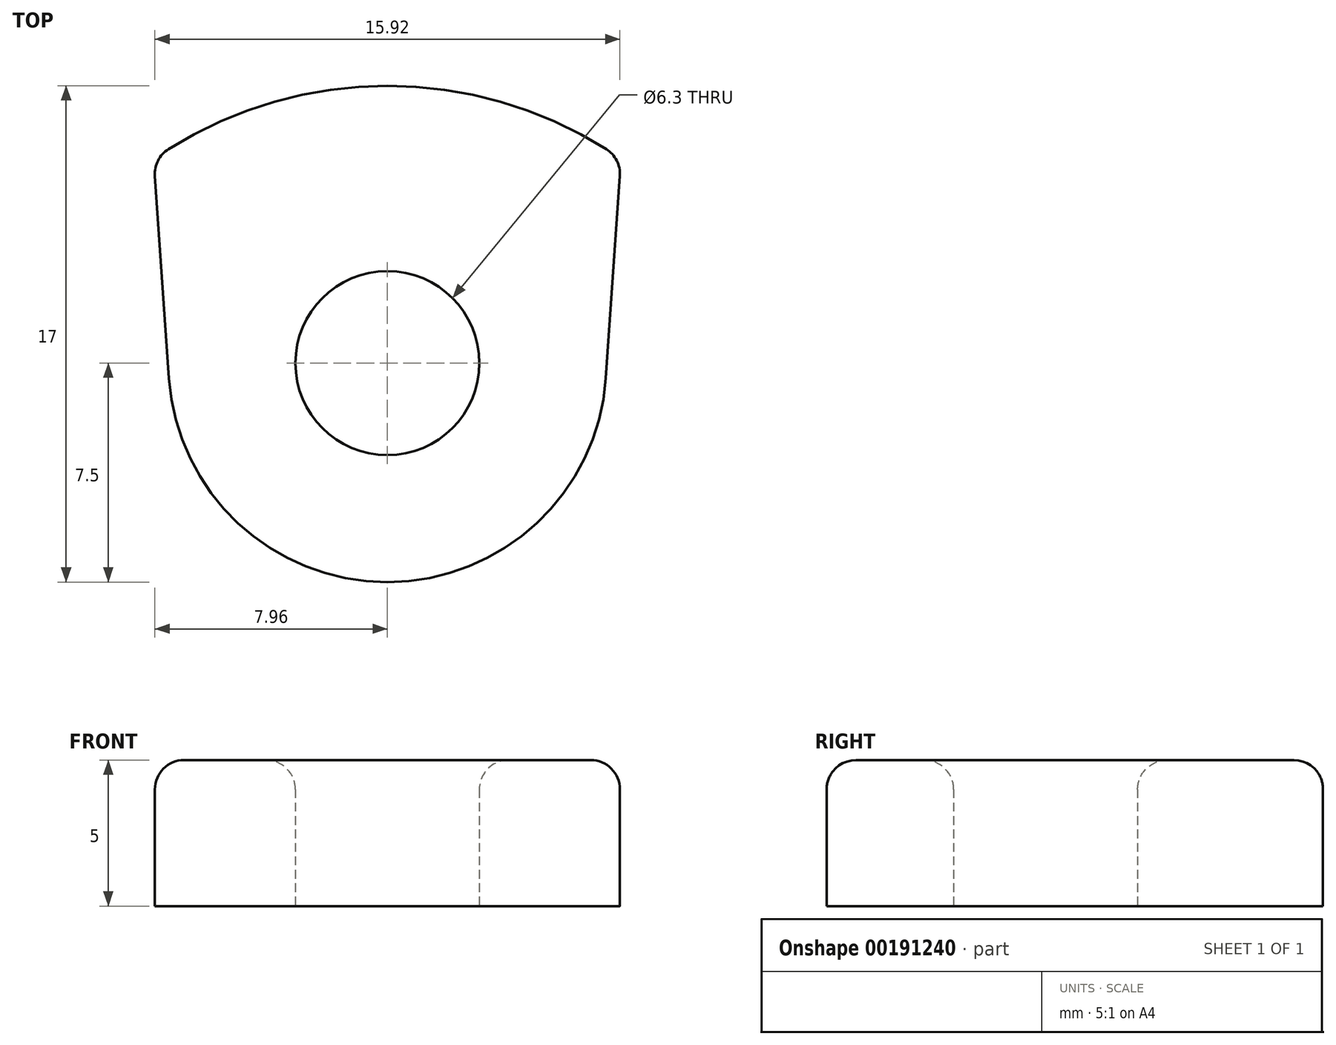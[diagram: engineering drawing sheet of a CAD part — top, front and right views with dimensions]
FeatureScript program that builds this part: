
annotation { "Feature Type Name" : "Feature", "Feature Type Description" : "" }
export const myFeature = defineFeature(function(context is Context, id is Id, definition is map)
    precondition{}
    {
        {
            var Q0;
            Q0=qCreatedBy(makeId("Top.planeOp"),FACE);
            var sketch = newSketch(context, id + "F0", { "sketchPlane" : qUnion([Q0])});
            skCircle(sketch, "E0", {"center": v(0, 0) * mm, "radius": 3.15 * mm});
            skArc(sketch, "E1", {"start": v(-7.48, -0.52) * mm, "mid": v(0, -7.5) * mm, "end": v(7.48, -0.52) * mm});
            skLineSegment(sketch, "E2", {"start": v(-8, 7) * mm, "end": v(0, 7) * mm, "construction": true});
            skLineSegment(sketch, "E3", {"start": v(-8, 7) * mm, "end": v(-7.48, -0.52) * mm});
            skLineSegment(sketch, "E4.MirrorCS", {"start": v(8, 7) * mm, "end": v(0, 7) * mm, "construction": true});
            skLineSegment(sketch, "E5.MirrorCS", {"start": v(8, 7) * mm, "end": v(7.48, -0.52) * mm});
            skLineSegment(sketch, "E6", {"start": v(0, 7) * mm, "end": v(0, 9.5) * mm, "construction": true});
            skArc(sketch, "E7", {"start": v(8, 7) * mm, "mid": v(0, 9.5) * mm, "end": v(-8, 7) * mm});
            skSolve(sketch);
        }
        {
            var Q0;
            Q0 = qSketchRegion(id + "F0", true);
            extrude(context, id + "F1", {"entities" : qUnion([Q0]), "depth" : 5 * mm});
        }
        {
            var Q0;
            Q0=makeQuery(id+"F1.opExtrude","SWEPT_EDGE",EDGE,{"disambiguationData":[OSD([sQuery(id+"F0.wireOp",EDGE,"E3"),sQuery(id+"F0.wireOp",EDGE,"E7")])]});
            var Q1;
            Q1=makeQuery(id+"F1.opExtrude","CAP_EDGE",EDGE,{"disambiguationData":[OSD([sQuery(id+"F0.wireOp",EDGE,"E1")])],"isStart":false});
            var Q2;
            Q2=makeQuery(id+"F1.opExtrude","CAP_EDGE",EDGE,{"disambiguationData":[OSD([sQuery(id+"F0.wireOp",EDGE,"E7")])],"isStart":false});
            var Q3;
            Q3=makeQuery(id+"F1.opExtrude","SWEPT_EDGE",EDGE,{"disambiguationData":[OSD([sQuery(id+"F0.wireOp",EDGE,"E5.MirrorCS"),sQuery(id+"F0.wireOp",EDGE,"E7")])]});
            var Q4;
            Q4=makeQuery(id+"F1.opExtrude","CAP_EDGE",EDGE,{"disambiguationData":[OSD([sQuery(id+"F0.wireOp",EDGE,"E0")])],"isStart":false});
            fillet(context, id + "F2", {"entities" : qUnion([Q0, Q1, Q2, Q3, Q4]), "radius" : 1 * mm, "tangentPropagation" : true, "allowEdgeOverflow" : false});
        }
    });
